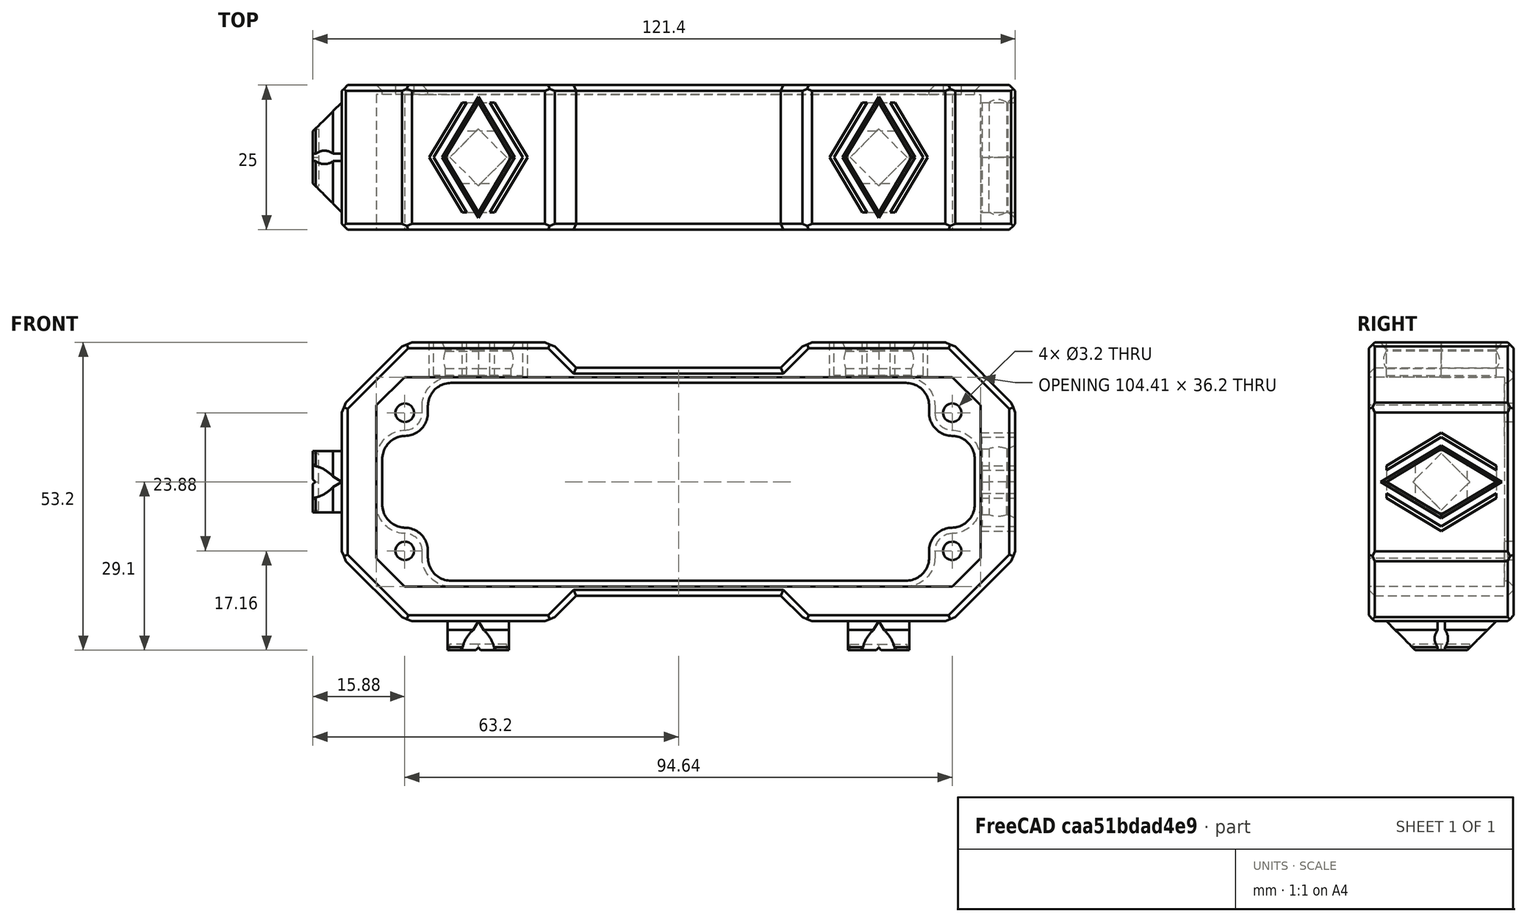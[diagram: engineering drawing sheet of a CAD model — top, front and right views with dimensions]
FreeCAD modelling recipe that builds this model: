
FCSTD DOCUMENT  (FreeCAD 1.1R20251031 (Git shallow))
Label: K93-10436-H7-L120_DockLink_Frame_example_mirrored
License: All rights reserved
LicenseURL: https://en.wikipedia.org/wiki/All_rights_reserved
objects: App::Link×7, PartDesign::Chamfer×2, Assembly::JointGroup×1, Part::MultiFuse×1, App::Point×1, PartDesign::FeatureBase×1, PartDesign::Body×1, Part::Mirroring×1
note: 11 computed .brp shape members not serialized (recipe doc carries the construction recipe); baked Part::Feature solids carry a one-line shape summary decoded from their .brp
EXTERNAL_REF file=K93-10436-H7-L120_DockLink_Frame.FCStd obj=Body
EXTERNAL_REF file=../../FreeCAD_DElements/DockLink/DockLink_male.FCStd obj=Body
EXTERNAL_REF file=../../FreeCAD_DElements/DockLink/DockLink_female.FCStd obj=Body

FEATURE [Assembly::JointGroup] Joints
FEATURE [App::Link] K93_10436_H7_L120_DockLink_Frame  label="K93-10436-H7-L120_DockLink_Frame"
  LinkPlacement = pos=(0,-10.9,-10.9) rot=(1,0,0;1.5708rad)
  LinkedObject = -> <external K93-10436-H7-L120_DockLink_Frame.FCStd>#Body
  Placement = pos=(0,-10.9,-10.9) rot=(1,0,0;1.5708rad)
FEATURE [App::Link] Body_DockLink_male
  LinkPlacement = pos=(34.6042,3.94077e-06,-35) rot=(1,0,0;3.14159rad)
  LinkedObject = -> <external ../../FreeCAD_DElements/DockLink/DockLink_male.FCStd>#Body
  Placement = pos=(34.6042,3.94077e-06,-35) rot=(1,0,0;3.14159rad)
FEATURE [App::Link] Body_DockLink_male001
  LinkPlacement = pos=(-34.6042,3.94077e-06,-35) rot=(0,1,0;3.14159rad)
  LinkedObject = -> <external ../../FreeCAD_DElements/DockLink/DockLink_male.FCStd>#Body
  Placement = pos=(-34.6042,3.94077e-06,-35) rot=(0,1,0;3.14159rad)
FEATURE [App::Link] Body_DockLink_male002
  LinkPlacement = pos=(-58.2042,-1.22189e-07,-10.9) rot=(0,1,0;4.71239rad)
  LinkedObject = -> <external ../../FreeCAD_DElements/DockLink/DockLink_male.FCStd>#Body
  Placement = pos=(-58.2042,-1.22189e-07,-10.9) rot=(0,1,0;4.71239rad)
FEATURE [App::Link] Body_DockLink_female
  LinkPlacement = pos=(34.6042,-3.17362e-06,7.2) rot=(1,0,0;0rad)
  LinkedObject = -> <external ../../FreeCAD_DElements/DockLink/DockLink_female.FCStd>#Body
  Placement = pos=(34.6042,-3.17362e-06,7.2) rot=(1,0,0;0rad)
FEATURE [App::Link] Body_DockLink_female002
  LinkPlacement = pos=(-34.6042,-3.17362e-06,7.2) rot=(1,0,0;0rad)
  LinkedObject = -> <external ../../FreeCAD_DElements/DockLink/DockLink_female.FCStd>#Body
  Placement = pos=(-34.6042,-3.17362e-06,7.2) rot=(1,0,0;0rad)
FEATURE [App::Link] Body_DockLink_female003
  LinkPlacement = pos=(52.2042,-1.22189e-07,-10.9) rot=(0,1,0;1.5708rad)
  LinkedObject = -> <external ../../FreeCAD_DElements/DockLink/DockLink_female.FCStd>#Body
  Placement = pos=(52.2042,-1.22189e-07,-10.9) rot=(0,1,0;1.5708rad)
FEATURE [Part::MultiFuse] Fusion
  Refine = true
  Shapes = -> [K93_10436_H7_L120_DockLink_Frame,Body_DockLink_male,Body_DockLink_male001,Body_DockLink_male002,Body_DockLink_female,Body_DockLink_female002,Body_DockLink_female003]
FEATURE [App::Point] Origin005  label="Origin006"
  Role = Origin
FEATURE [PartDesign::FeatureBase] BaseFeature
  BaseFeature = -> Fusion
  Suppressed = false
FEATURE [PartDesign::Chamfer] Chamfer
  Angle = 45
  Base = -> BaseFeature [Edge186,Edge341,Edge191,Edge207,Edge211,Edge212,Edge219,Edge234,Edge349,Edge348,Edge347,Edge346,Edge345,Edge344,Edge343,Edge342,Edge236,Edge221,Edge214,Edge210,Edge206,Edge193,Edge184,Edge494,Edge376,Edge367,Edge356,Edge354,Edge350,Edge357,Edge365,Edge493,Edge49]
  BaseFeature = -> BaseFeature
  ChamferType = 0
  FlipDirection = false
  Refine = true
  Size = 1
  Size2 = 1
  SupportTransform = false
  Suppressed = false
  UseAllEdges = false
FEATURE [PartDesign::Chamfer] Chamfer001
  Angle = 45
  Base = -> Chamfer [Edge351,Edge341,Edge338,Edge312,Edge308,Edge299,Edge287,Edge285,Edge289,Edge321,Edge325,Edge337]
  BaseFeature = -> Chamfer
  ChamferType = 0
  FlipDirection = false
  Refine = true
  Size = 1
  Size2 = 1
  SupportTransform = false
  Suppressed = false
  UseAllEdges = false
FEATURE [PartDesign::Body] Body
  AllowCompound = true
  BaseFeature = -> Fusion
  Group = -> [BaseFeature,Chamfer,Chamfer001]
  Origin = -> Origin004
  Tip = -> Chamfer001
FEATURE [Part::Mirroring] Part__Mirroring  label="Body (Mirror #1)"
  Base = (0,0,0)
  Normal = (0,1,0)
  Source = -> Body

RESOLVED EXTERNAL PARTS (link-assembly join: the EXTERNAL_REF files above that resolve inside this repo's crawl, each included once):
---- part K93-10436-H7-L120_DockLink_Frame.FCStd = doc fcstd_11a9cadb3d35 ----
FCSTD DOCUMENT  (FreeCAD 1.1R20251111 (Git shallow))
Label: K93-10436-H7-L120_DockLink_Frame
License: All rights reserved
LicenseURL: https://en.wikipedia.org/wiki/All_rights_reserved
objects: Sketcher::SketchObject×6, PartDesign::Pocket×4, App::FeaturePython×3, Part::Feature×3, PartDesign::Pad×2, PartDesign::Mirrored×2, App::Point×1, App::DocumentObjectGroupPython×1, App::VarSet×1, PartDesign::Fillet×1, PartDesign::Body×1
note: 41 computed .brp shape members not serialized (recipe doc carries the construction recipe); baked Part::Feature solids carry a one-line shape summary decoded from their .brp

FEATURE [App::Point] Origin001
  Role = Origin
FEATURE [App::FeaturePython] Layer  label="0"  # WARN: FeaturePython — macro-defined, semantics opaque (R4)
FEATURE [App::FeaturePython] Layer001  label="none"  # WARN: FeaturePython — macro-defined, semantics opaque (R4)
FEATURE [App::FeaturePython] Layer002  label="Shape2DView"  # WARN: FeaturePython — macro-defined, semantics opaque (R4)
FEATURE [App::DocumentObjectGroupPython] LayerContainer  label="Layers"  # scripted group (container) (typed FeaturePython)
  Group = -> [Layer,Layer002,Layer001]
FEATURE [Part::Feature] Wire
  shape: bbox 3.2 x 3.2 x 2e-07 mm, 0 faces, 0 solids (baked)
FEATURE [Part::Feature] Wire001
  shape: bbox 3.2 x 3.2 x 2e-07 mm, 0 faces, 0 solids (baked)
FEATURE [Part::Feature] Wire002
  shape: bbox 98.17 x 35.99 x 2e-07 mm, 0 faces, 0 solids (baked)
FEATURE [App::VarSet] VarSet
  depth_feet = 26
  gap = 0.1
  thickness_wall = 1.6
FEATURE [Sketcher::SketchObject] Sketch  label="panel_reference"
  ArcFitTolerance = 1e-06
  ExternalTypes = [0]
  FullyConstrained = true
  MakeInternals = false
  expr: Constraints[35] = VarSet.gap
  expr: Constraints[46] = VarSet.thickness_wall
  expr: Constraints[49] = VarSet.gap * 3
  expr: Constraints[50] = VarSet.gap * 2
  sketch-geometry (16):
    g0: LineSegment [constr] StartX=52.0042 StartY=0 StartZ=0 EndX=52.0042 EndY=12.17 EndZ=0
    g1: ArcOfCircle [constr] CenterX=50.0143 CenterY=12.1873 CenterZ=0 NormalX=0 NormalY=0 NormalZ=1 AngleXU=0 Radius=1.99 StartAngle=6.27451 EndAngle=7.06367
    g2: LineSegment [constr] StartX=51.4283 StartY=13.5875 StartZ=0 EndX=47.5958 EndY=17.42 EndZ=0
    g3: ArcOfCircle [constr] CenterX=46.1874 CenterY=16 CenterZ=0 NormalX=0 NormalY=0 NormalZ=1 AngleXU=0 Radius=2 StartAngle=0.789489 EndAngle=1.57449
    g4: LineSegment [constr] StartX=46.18 StartY=18 StartZ=0 EndX=0 EndY=18 EndZ=0
    g5: Circle [constr] CenterX=47.32 CenterY=11.94 CenterZ=0 NormalX=0 NormalY=0 NormalZ=1 AngleXU=0 Radius=1.61
    g6: LineSegment StartX=52.2042 StartY=0 StartZ=0 EndX=58.2042 EndY=0 EndZ=0
    g7: LineSegment StartX=52.2042 StartY=0 StartZ=0 EndX=52.2042 EndY=13.2359 EndZ=0
    g8: LineSegment StartX=58.2042 StartY=0 StartZ=0 EndX=58.2042 EndY=13 EndZ=0
    g9: LineSegment StartX=47.3401 StartY=18.1 StartZ=0 EndX=52.2042 EndY=13.2359 EndZ=0
    g10: LineSegment StartX=47.1042 StartY=24.1 StartZ=0 EndX=58.2042 EndY=13 EndZ=0
    g11: LineSegment StartX=17.7042 StartY=19.7 StartZ=0 EndX=22.1042 EndY=24.1 EndZ=0
    g12: LineSegment StartX=22.1042 StartY=24.1 StartZ=0 EndX=47.1042 EndY=24.1 EndZ=0
    g13: LineSegment StartX=47.3401 StartY=18.1 StartZ=0 EndX=0 EndY=18.1 EndZ=0
    g14: LineSegment StartX=17.7042 StartY=19.7 StartZ=0 EndX=0 EndY=19.7 EndZ=0
    g15: LineSegment StartX=0 StartY=19.7 StartZ=0 EndX=0 EndY=18.1 EndZ=0
  constraints (52):
    c: Coincident(g3,g4)
    c: Coincident(g2,g3)
    c: Coincident(g1,g2)
    c: Coincident(g0,g1)
    c: PointOnObject(g4,g-2)
    c: Horizontal(g4)
    c: PointOnObject(g6,g-1)
    c: PointOnObject(g6,g-1)
    c: Distance(g4,g-1) = 18
    c: Vertical(g0)
    c: DistanceY(g-1,g0) = 12.17
    c: Distance(g1,g0) = 1.53
    c: Angle(g2,g0) = 2.35619
    c: Distance(g2,g2) = 5.42
    c: Distance(g3,g2) = 1.53
    c: DistanceX(g4,g4) = 46.18
    c: DistanceY(g-1,g2) = 17.42
    c: DistanceY(g-1,g5) = 11.94
    c: Diameter(g5) = 3.22
    c: DistanceX(g-1,g5) = 47.32
    c: Radius(g3) = 2
    c: Radius(g1) = 1.99
    c: PointOnObject(g0,g-1)
    c: Coincident(g7,g6)
    c: Vertical(g7)
    c: Coincident(g8,g6)
    c: Vertical(g8)
    c: Parallel(g2,g9)
    c: Parallel(g9,g10)
    c: Coincident(g9,g7)
    c: Coincident(g10,g8)
    c: Coincident(g12,g11)
    c: Horizontal(g12)
    c: Distance(g9,g12) = 6
    c: Coincident(g10,g12)
    c: Distance(g9,g4) = 0.1
    c: DistanceX(g12,g12) = 25
    c: Coincident(g13,g9)
    c: PointOnObject(g13,g-2)
    c: Horizontal(g13)
    c: Coincident(g14,g11)
    c: PointOnObject(g14,g-2)
    c: Horizontal(g14)
    c: Coincident(g15,g14)
    c: Coincident(g15,g13)
    c: Angle(g11,g14) = 2.35619
    c: DistanceY(g15,g15) = 1.6
    c: Distance(g6,g6) = 6
    c: DistanceY(g8,g8) = 13
    c: Distance(g9,g2) = 0.3
    c: Distance(g0,g7) = 0.2
    c: Distance(g9,g10) = 4.07586
FEATURE [PartDesign::Pad] Pad
  Direction = (0,0,1)
  Length = 23.4
  Length2 = 10
  Profile = -> Sketch
  ReferenceAxis = -> Sketch [N_Axis]
  Refine = true
  Reversed = true
  SideType = 0
  Suppressed = false
  Type = 0
  Type2 = 0
FEATURE [PartDesign::Mirrored] Mirrored
  BaseFeature = -> Pad
  MirrorPlane = -> YZ_Plane
  Refine = true
  Suppressed = false
  TransformMode = 1
FEATURE [PartDesign::Mirrored] Mirrored001
  BaseFeature = -> Mirrored
  MirrorPlane = -> XZ_Plane
  Refine = true
  Suppressed = false
  TransformMode = 1
FEATURE [Sketcher::SketchObject] Sketch001  label="Sketch_Frontplate"
  ArcFitTolerance = 1e-06
  AttachmentSupport = -> [Mirrored001]
  ExternalGeometry = -> [Mirrored001]
  ExternalTypes = [0,0,0,0,0,0,0,0,0,0,0,0,0,0,0,0]
  FullyConstrained = true
  MakeInternals = false
  MapMode = 5
  Placement = pos=(0,0,-7.9e-15) rot=(0,0,1;0rad)
  sketch-geometry (25):
    g0: LineSegment [constr] StartX=-47.32 StartY=11.94 StartZ=0 EndX=-47.32 EndY=-11.94 EndZ=0
    g1: LineSegment [constr] StartX=-47.32 StartY=-11.94 StartZ=0 EndX=47.32 EndY=-11.94 EndZ=0
    g2: LineSegment [constr] StartX=47.32 StartY=-11.94 StartZ=0 EndX=47.32 EndY=11.94 EndZ=0
    g3: LineSegment [constr] StartX=47.32 StartY=11.94 StartZ=0 EndX=-47.32 EndY=11.94 EndZ=0
    g4: GeomPoint [constr] X=0 Y=0 Z=0
    g5: Circle CenterX=-47.32 CenterY=11.94 CenterZ=0 NormalX=0 NormalY=0 NormalZ=1 AngleXU=0 Radius=1.6
    g6: Circle CenterX=-47.32 CenterY=-11.94 CenterZ=0 NormalX=0 NormalY=0 NormalZ=1 AngleXU=0 Radius=1.6
    g7: Circle CenterX=47.32 CenterY=11.94 CenterZ=0 NormalX=0 NormalY=0 NormalZ=1 AngleXU=0 Radius=1.6
    g8: Circle CenterX=47.32 CenterY=-11.94 CenterZ=0 NormalX=0 NormalY=0 NormalZ=1 AngleXU=0 Radius=1.6
    g9: LineSegment StartX=-43.32 StartY=17.1 StartZ=0 EndX=43.32 EndY=17.1 EndZ=0
    g10: LineSegment StartX=-51.2042 StartY=7.94 StartZ=0 EndX=-51.2042 EndY=-7.94 EndZ=0
    g11: LineSegment StartX=51.2042 StartY=7.94 StartZ=0 EndX=51.2042 EndY=-7.94 EndZ=0
    g12: LineSegment StartX=-43.32 StartY=-17.1 StartZ=0 EndX=43.32 EndY=-17.1 EndZ=0
    g13: ArcOfCircle CenterX=-47.32 CenterY=11.94 CenterZ=0 NormalX=0 NormalY=0 NormalZ=1 AngleXU=0 Radius=4 StartAngle=4.71239 EndAngle=6.28319
    g14: ArcOfCircle CenterX=-47.32 CenterY=-11.94 CenterZ=0 NormalX=0 NormalY=0 NormalZ=1 AngleXU=0 Radius=4 StartAngle=0 EndAngle=1.5708
    g15: ArcOfCircle CenterX=47.32 CenterY=-11.94 CenterZ=0 NormalX=0 NormalY=0 NormalZ=1 AngleXU=0 Radius=4 StartAngle=1.5708 EndAngle=3.14159
    g16: ArcOfCircle CenterX=47.32 CenterY=11.94 CenterZ=0 NormalX=0 NormalY=0 NormalZ=1 AngleXU=0 Radius=4 StartAngle=3.14159 EndAngle=4.71239
    g17: LineSegment StartX=43.32 StartY=11.94 StartZ=0 EndX=43.32 EndY=17.1 EndZ=0
    g18: LineSegment StartX=-43.32 StartY=11.94 StartZ=0 EndX=-43.32 EndY=17.1 EndZ=0
    g19: LineSegment StartX=-47.32 StartY=7.94 StartZ=0 EndX=-51.2042 EndY=7.94 EndZ=0
    g20: LineSegment StartX=-47.32 StartY=-7.94 StartZ=0 EndX=-51.2042 EndY=-7.94 EndZ=0
    g21: LineSegment StartX=-43.32 StartY=-17.1 StartZ=0 EndX=-43.32 EndY=-11.94 EndZ=0
    g22: LineSegment StartX=47.32 StartY=7.94 StartZ=0 EndX=51.2042 EndY=7.94 EndZ=0
    g23: LineSegment StartX=47.32 StartY=-7.94 StartZ=0 EndX=51.2042 EndY=-7.94 EndZ=0
    g24: LineSegment StartX=43.32 StartY=-11.94 StartZ=0 EndX=43.32 EndY=-17.1 EndZ=0
  constraints (66):
    c: Coincident(g0,g1)
    c: Coincident(g1,g2)
    c: Coincident(g2,g3)
    c: Coincident(g3,g0)
    c: Vertical(g0)
    c: Vertical(g2)
    c: Horizontal(g1)
    c: Horizontal(g3)
    c: Symmetric(g2,g0,g4)
    c: Coincident(g4,g-1)
    c: Distance(g3,g-1) = 11.94
    c: Distance(g-2,g2) = 47.32
    c: Coincident(g5,g3)
    c: Coincident(g6,g0)
    c: Coincident(g7,g2)
    c: Coincident(g8,g1)
    c: Equal(g8,g7)
    c: Equal(g7,g6)
    c: Equal(g6,g5)
    c: Diameter(g5) = 3.2
    c: Vertical(g10)
    c: Vertical(g11)
    c: Symmetric(g9,g9,g-2)
    c: Symmetric(g12,g12,g-2)
    c: Coincident(g13,g3)
    c: PointOnObject(g13,g0)
    c: PointOnObject(g13,g3)
    c: Radius(g13) = 4
    c: Coincident(g14,g0)
    c: PointOnObject(g14,g0)
    c: PointOnObject(g14,g1)
    c: Coincident(g15,g1)
    c: PointOnObject(g15,g1)
    c: PointOnObject(g15,g2)
    c: Coincident(g16,g2)
    c: PointOnObject(g16,g2)
    c: PointOnObject(g16,g3)
    c: Coincident(g17,g16)
    c: PointOnObject(g17,g9)
    c: Vertical(g17)
    c: Vertical(g9,g17)
    c: Equal(g16,g15)
    c: Equal(g15,g14)
    c: Tangent(g18,g13) = -1.5708
    c: Coincident(g18,g9)
    c: Coincident(g19,g13)
    c: Coincident(g19,g10)
    c: Coincident(g20,g14)
    c: Coincident(g20,g10)
    c: Coincident(g21,g12)
    c: Coincident(g21,g14)
    c: Coincident(g22,g16)
    c: Coincident(g22,g11)
    c: Coincident(g23,g15)
    c: Coincident(g23,g11)
    c: Coincident(g24,g15)
    c: Coincident(g24,g12)
    c: Vertical(g24)
    c: Horizontal(g22)
    c: Horizontal(g23)
    c: Horizontal(g19)
    c: Horizontal(g20)
    c: Distance(g10,g-18) = 7
    c: Distance(g-6,g9) = 2.6
    c: Distance(g-14,g12) = 2.6
    c: Distance(g-10,g11) = 7
FEATURE [PartDesign::Pad] Pad001
  BaseFeature = -> Mirrored001
  Direction = (0,0,1)
  Length = 1.6
  Length2 = 10
  Profile = -> Sketch001
  ReferenceAxis = -> Sketch001 [N_Axis]
  Refine = true
  SideType = 0
  Suppressed = false
  Type = 0
  Type2 = 0
FEATURE [PartDesign::Fillet] Fillet
  Base = -> Pad001 [Edge112,Edge99,Edge100,Edge103,Edge104,Edge107,Edge108,Edge111]
  BaseFeature = -> Pad001
  Radius = 4
  Refine = true
  SupportTransform = false
  Suppressed = false
  UseAllEdges = false
FEATURE [Sketcher::SketchObject] Sketch002
  ArcFitTolerance = 1e-06
  AttachmentSupport = -> [Fillet]
  ExternalGeometry = -> [Fillet]
  ExternalTypes = [0,0]
  FullyConstrained = true
  MakeInternals = false
  MapMode = 5
  Placement = pos=(6.8e-15,24.1,0) rot=(0,0.707107,0.707107;3.14159rad)
FEATURE [PartDesign::Pocket] Pocket
  BaseFeature = -> Fillet
  Direction = (0,-1,2e-16)
  Length = 6
  Length2 = 5
  Profile = -> Sketch002
  ReferenceAxis = -> Sketch002 [N_Axis]
  Refine = true
  SideType = 0
  Suppressed = false
  Type = 0
  Type2 = 0
FEATURE [Sketcher::SketchObject] Sketch003
  ArcFitTolerance = 1e-06
  AttachmentSupport = -> [Pocket]
  ExternalGeometry = -> [Pocket]
  ExternalTypes = [0,0]
  FullyConstrained = true
  MakeInternals = false
  MapMode = 5
  Placement = pos=(6.8e-15,-24.1,-1.06e-14) rot=(1,0,0;1.5708rad)
FEATURE [PartDesign::Pocket] Pocket001
  BaseFeature = -> Pocket
  Direction = (0,1,-2e-16)
  Length = 6
  Length2 = 5
  Profile = -> Sketch003
  ReferenceAxis = -> Sketch003 [N_Axis]
  Refine = true
  SideType = 0
  Suppressed = false
  Type = 0
  Type2 = 0
FEATURE [Sketcher::SketchObject] Sketch004
  ArcFitTolerance = 1e-06
  AttachmentSupport = -> [Pocket001]
  ExternalGeometry = -> [Pocket001]
  ExternalTypes = [0,0,0,0]
  FullyConstrained = true
  MakeInternals = false
  MapMode = 5
  Placement = pos=(-58.2042,0,-1.7e-14) rot=(0.57735,-0.57735,-0.57735;2.0944rad)
  sketch-geometry (8):
    g0: LineSegment [constr] StartX=-13 StartY=1.6 StartZ=0 EndX=13 EndY=-23.4 EndZ=0
    g1: LineSegment [constr] StartX=13 StartY=1.6 StartZ=0 EndX=-13 EndY=-23.4 EndZ=0
    g2: GeomPoint [constr] X=0 Y=-10.9 Z=0
    g3: LineSegment StartX=-12.5 StartY=1.6 StartZ=0 EndX=-12.5 EndY=-23.4 EndZ=0
    g4: LineSegment StartX=-12.5 StartY=-23.4 StartZ=0 EndX=12.5 EndY=-23.4 EndZ=0
    g5: LineSegment StartX=12.5 StartY=-23.4 StartZ=0 EndX=12.5 EndY=1.6 EndZ=0
    g6: LineSegment StartX=12.5 StartY=1.6 StartZ=0 EndX=-12.5 EndY=1.6 EndZ=0
    g7: GeomPoint [constr] X=0 Y=-10.9 Z=0
  constraints (17):
    c: Coincident(g0,g-3)
    c: Coincident(g0,g-6)
    c: Coincident(g1,g-4)
    c: Coincident(g1,g-5)
    c: Symmetric(g1,g1,g2)
    c: Coincident(g3,g4)
    c: Coincident(g4,g5)
    c: Coincident(g5,g6)
    c: Coincident(g6,g3)
    c: Vertical(g3)
    c: Vertical(g5)
    c: Horizontal(g4)
    c: Horizontal(g6)
    c: Symmetric(g5,g3,g7)
    c: Coincident(g7,g2)
    c: Equal(g5,g6)
    c: DistanceX(g6,g6) = 25
FEATURE [PartDesign::Pocket] Pocket002
  BaseFeature = -> Pocket001
  Direction = (1,0,0)
  Length = 6
  Length2 = 5
  Profile = -> Sketch004
  ReferenceAxis = -> Sketch004 [N_Axis]
  Refine = true
  SideType = 0
  Suppressed = false
  Type = 0
  Type2 = 0
FEATURE [Sketcher::SketchObject] Sketch005
  ArcFitTolerance = 1e-06
  AttachmentSupport = -> [Pocket002]
  ExternalGeometry = -> [Pocket002]
  ExternalTypes = [0,0,0,0]
  FullyConstrained = true
  MakeInternals = false
  MapMode = 5
  Placement = pos=(58.2042,0,0) rot=(0.57735,0.57735,0.57735;2.0944rad)
  sketch-geometry (8):
    g0: LineSegment [constr] StartX=-13 StartY=-23.4 StartZ=0 EndX=13 EndY=1.6 EndZ=0
    g1: LineSegment [constr] StartX=13 StartY=-23.4 StartZ=0 EndX=-13 EndY=1.6 EndZ=0
    g2: GeomPoint [constr] X=3e-16 Y=-10.9 Z=0
    g3: LineSegment StartX=-12.5 StartY=1.6 StartZ=0 EndX=-12.5 EndY=-23.4 EndZ=0
    g4: LineSegment StartX=-12.5 StartY=-23.4 StartZ=0 EndX=12.5 EndY=-23.4 EndZ=0
    g5: LineSegment StartX=12.5 StartY=-23.4 StartZ=0 EndX=12.5 EndY=1.6 EndZ=0
    g6: LineSegment StartX=12.5 StartY=1.6 StartZ=0 EndX=-12.5 EndY=1.6 EndZ=0
    g7: GeomPoint [constr] X=3e-16 Y=-10.9 Z=0
  constraints (17):
    c: Coincident(g0,g-6)
    c: Coincident(g0,g-5)
    c: Coincident(g1,g-4)
    c: Coincident(g1,g-3)
    c: Symmetric(g1,g1,g2)
    c: Coincident(g3,g4)
    c: Coincident(g4,g5)
    c: Coincident(g5,g6)
    c: Coincident(g6,g3)
    c: Vertical(g3)
    c: Vertical(g5)
    c: Horizontal(g4)
    c: Horizontal(g6)
    c: Symmetric(g5,g3,g7)
    c: Coincident(g7,g2)
    c: Equal(g5,g6)
    c: DistanceX(g6,g6) = 25
FEATURE [PartDesign::Pocket] Pocket003
  BaseFeature = -> Pocket002
  Direction = (-1,0,0)
  Length = 6
  Length2 = 5
  Profile = -> Sketch005
  ReferenceAxis = -> Sketch005 [N_Axis]
  Refine = true
  SideType = 0
  Suppressed = false
  Type = 0
  Type2 = 0
FEATURE [PartDesign::Body] Body  label="K93-10436-H7-L120_DockLink_Frame"
  AllowCompound = true
  Group = -> [Sketch,Pad,Mirrored,Mirrored001,Sketch001,Pad001,Fillet,Sketch002,Pocket,Sketch003,Pocket001,Sketch004,Pocket002,Sketch005,Pocket003]
  Origin = -> Origin
  Tip = -> Pocket003
